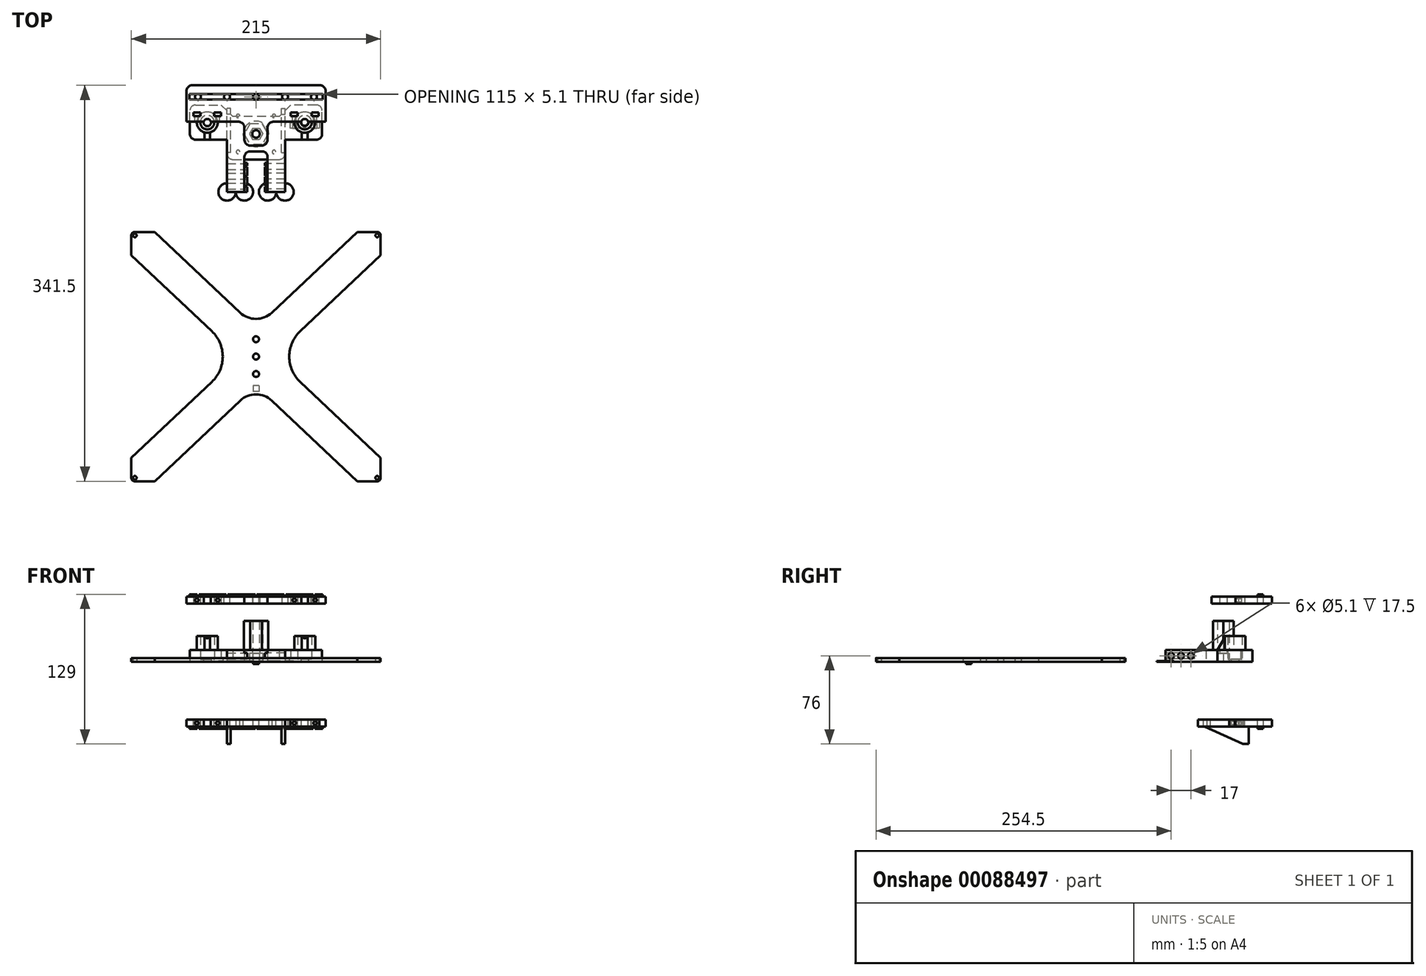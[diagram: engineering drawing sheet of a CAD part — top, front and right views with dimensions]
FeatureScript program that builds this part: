
annotation { "Feature Type Name" : "Feature", "Feature Type Description" : "" }
export const myFeature = defineFeature(function(context is Context, id is Id, definition is map)
    precondition{}
    {
        {
            var Q0;
            Q0=qCreatedBy(makeId("Top.planeOp"),FACE);
            var sketch = newSketch(context, id + "F0", { "sketchPlane" : qUnion([Q0])});
            skArc(sketch, "E0", {"start": v(0, -3.25) * mm, "mid": v(3.25, 0) * mm, "end": v(0, 3.25) * mm});
            skCircle(sketch, "E1", {"center": v(42, 10) * mm, "radius": 3.25 * mm});
            skLineSegment(sketch, "E2", {"start": v(0, -15) * mm, "end": v(5, -15) * mm});
            skLineSegment(sketch, "E3", {"start": v(10, -20) * mm, "end": v(10, -50) * mm});
            skLineSegment(sketch, "E4", {"start": v(10, -50) * mm, "end": v(25, -50) * mm});
            skLineSegment(sketch, "E5", {"start": v(25, -50) * mm, "end": v(25, -5) * mm});
            skLineSegment(sketch, "E6", {"start": v(25, -5) * mm, "end": v(52, -5) * mm});
            skLineSegment(sketch, "E7", {"start": v(57, 0) * mm, "end": v(57, 20) * mm});
            skLineSegment(sketch, "E8", {"start": v(52, 25) * mm, "end": v(30, 25) * mm});
            skLineSegment(sketch, "E9", {"start": v(30, 25) * mm, "end": v(20, 15) * mm});
            skLineSegment(sketch, "E10", {"start": v(20, 15) * mm, "end": v(0, 15) * mm});
            skPoint(sketch, "E11.visualSharp", {"position": v(10, -15) * mm});
            skArc(sketch, "E11.filletArc", {"start": v(10, -20) * mm, "mid": v(8.54, -16.46) * mm, "end": v(5, -15) * mm});
            skLineSegment(sketch, "E12", {"start": v(0, 15) * mm, "end": v(0, 3.25) * mm});
            skCircle(sketch, "E13.cCircle", {"center": v(0, 0) * mm, "radius": 5 * mm, "construction": true});
            skLineSegment(sketch, "E13.0", {"start": v(-2.89, 5) * mm, "end": v(2.89, 5) * mm, "construction": true});
            skLineSegment(sketch, "E13.1", {"start": v(2.89, 5) * mm, "end": v(5.77, 0) * mm, "construction": true});
            skLineSegment(sketch, "E13.2", {"start": v(5.77, 0) * mm, "end": v(2.89, -5) * mm, "construction": true});
            skLineSegment(sketch, "E13.3", {"start": v(2.89, -5) * mm, "end": v(-2.89, -5) * mm, "construction": true});
            skLineSegment(sketch, "E13.4", {"start": v(-2.89, -5) * mm, "end": v(-5.77, 0) * mm, "construction": true});
            skLineSegment(sketch, "E13.5", {"start": v(-5.77, 0) * mm, "end": v(-2.89, 5) * mm, "construction": true});
            skPoint(sketch, "E13.0.midPoint", {"position": v(0, 5) * mm});
            skLineSegment(sketch, "E14.trimOffspring", {"start": v(0, -3.25) * mm, "end": v(0, -15) * mm});
            skPoint(sketch, "E15.visualSharp", {"position": v(57, -5) * mm});
            skArc(sketch, "E15.filletArc", {"start": v(52, -5) * mm, "mid": v(55.54, -3.54) * mm, "end": v(57, 0) * mm});
            skPoint(sketch, "E16.visualSharp", {"position": v(57, 25) * mm});
            skArc(sketch, "E16.filletArc", {"start": v(57, 20) * mm, "mid": v(55.54, 23.54) * mm, "end": v(52, 25) * mm});
            skSolve(sketch);
        }
        {
            var Q0;
            Q0=makeQuery(id+"F0.imprint","IMPRINT",FACE,{"disambiguationData":[TD([[makeQuery(id+"F0.imprint","IMPRINT",EDGE,{"derivedFrom":sQuery(id+"F0.wireOp",EDGE,"E0")}),-1.0]])]});
            extrude(context, id + "F1", {"entities" : qUnion([Q0]), "depth" : 10 * mm});
        }
        {
            var Q0;
            Q0=makeQuery(id+"F1.opExtrude","CAP_FACE",FACE,{"disambiguationData":[OSD([sQuery(id+"F0.wireOp",EDGE,"E0"),sQuery(id+"F0.wireOp",EDGE,"E1"),sQuery(id+"F0.wireOp",EDGE,"E2"),sQuery(id+"F0.wireOp",EDGE,"E3"),sQuery(id+"F0.wireOp",EDGE,"E4"),sQuery(id+"F0.wireOp",EDGE,"E5"),sQuery(id+"F0.wireOp",EDGE,"E6"),sQuery(id+"F0.wireOp",EDGE,"E7"),sQuery(id+"F0.wireOp",EDGE,"E8"),sQuery(id+"F0.wireOp",EDGE,"E9"),sQuery(id+"F0.wireOp",EDGE,"E10"),sQuery(id+"F0.wireOp",EDGE,"E11.filletArc"),sQuery(id+"F0.wireOp",EDGE,"E12"),sQuery(id+"F0.wireOp",EDGE,"E14.trimOffspring"),sQuery(id+"F0.wireOp",EDGE,"E15.filletArc"),sQuery(id+"F0.wireOp",EDGE,"E16.filletArc")])],"isStart":false});
            var sketch = newSketch(context, id + "F2", { "sketchPlane" : qUnion([Q0])});
            skCircle(sketch, "E17", {"center": v(42, 10) * mm, "radius": 6.05 * mm});
            skCircle(sketch, "E18", {"center": v(42, 10) * mm, "radius": 9 * mm});
            skSolve(sketch);
        }
        {
            var Q0;
            Q0 = qSketchRegion(id + "F2", true);
            extrude(context, id + "F3", {"entities" : qUnion([Q0]), "operationType" : NewBodyOperationType.ADD, "depth" : 12 * mm});
        }
        {
            var Q0;
            {var subQ0=sQuery(id+"F0.wireOp",EDGE,"E9");var subQ1=sQuery(id+"F0.wireOp",EDGE,"E8");var subQ2=sQuery(id+"F0.wireOp",EDGE,"E16.filletArc");var subQ3=sQuery(id+"F0.wireOp",EDGE,"E7");var subQ4=sQuery(id+"F0.wireOp",EDGE,"E15.filletArc");var subQ5=sQuery(id+"F0.wireOp",EDGE,"E6");var subQ6=sQuery(id+"F0.wireOp",EDGE,"E5");var subQ7=sQuery(id+"F0.wireOp",EDGE,"E0");var subQ8=sQuery(id+"F0.wireOp",EDGE,"E2");var subQ9=sQuery(id+"F0.wireOp",EDGE,"E10");var subQ10=sQuery(id+"F0.wireOp",EDGE,"E3");var subQ11=sQuery(id+"F0.wireOp",EDGE,"E4");var subQ12=sQuery(id+"F0.wireOp",EDGE,"E11.filletArc");var subQ13=sQuery(id+"F0.wireOp",EDGE,"E12");var subQ14=sQuery(id+"F0.wireOp",EDGE,"E14.trimOffspring");Q0=makeQuery(id+"F3.boolean.opBoolean","SPLIT",FACE,{"disambiguationData":[TD([makeQuery(id+"F1.opExtrude","SWEPT_FACE",FACE,{"disambiguationData":[OSD([subQ7])]})])],"derivedFrom":makeQuery(id+"F1.opExtrude","CAP_FACE",FACE,{"disambiguationData":[OSD([subQ7,sQuery(id+"F0.wireOp",EDGE,"E1"),subQ8,subQ10,subQ11,subQ6,subQ5,subQ3,subQ1,subQ0,subQ9,subQ12,subQ13,subQ14,subQ4,subQ2])],"isStart":false})});}
            var sketch = newSketch(context, id + "F4", { "sketchPlane" : qUnion([Q0])});
            skArc(sketch, "E19.cCircle", {"start": v(0, -5) * mm, "mid": v(4.33, -2.5) * mm, "end": v(4.33, 2.5) * mm, "construction": true});
            skLineSegment(sketch, "E19.0", {"start": v(0, 5) * mm, "end": v(2.89, 5) * mm});
            skLineSegment(sketch, "E19.1", {"start": v(2.89, 5) * mm, "end": v(5.77, 0) * mm});
            skLineSegment(sketch, "E19.2", {"start": v(5.77, 0) * mm, "end": v(2.89, -5) * mm});
            skLineSegment(sketch, "E19.3", {"start": v(2.89, -5) * mm, "end": v(0, -5) * mm});
            skPoint(sketch, "E19.0.midPoint", {"position": v(0, 5) * mm});
            skArc(sketch, "E20.cCircle", {"start": v(0, -9) * mm, "mid": v(9, 0) * mm, "end": v(0, 9) * mm, "construction": true});
            skLineSegment(sketch, "E20.0", {"start": v(0, 9) * mm, "end": v(5.2, 9) * mm});
            skLineSegment(sketch, "E20.1", {"start": v(5.2, 9) * mm, "end": v(10.4, 0) * mm});
            skLineSegment(sketch, "E20.2", {"start": v(10.4, 0) * mm, "end": v(5.2, -9) * mm});
            skLineSegment(sketch, "E20.3", {"start": v(5.2, -9) * mm, "end": v(0, -9) * mm});
            skPoint(sketch, "E20.0.midPoint", {"position": v(0, 9) * mm});
            skLineSegment(sketch, "E21", {"start": v(0, 9) * mm, "end": v(0, 5) * mm});
            skLineSegment(sketch, "E22", {"start": v(0, -9.12) * mm, "end": v(0, -5) * mm});
            skSolve(sketch);
        }
        {
            var Q0;
            Q0 = qSketchRegion(id + "F4", true);
            extrude(context, id + "F5", {"entities" : qUnion([Q0]), "operationType" : NewBodyOperationType.ADD, "depth" : 25 * mm});
        }
        {
            var Q0;
            {var subQ0=sQuery(id+"F0.wireOp",EDGE,"E11.filletArc");var subQ2=sQuery(id+"F0.wireOp",EDGE,"E9");var subQ4=sQuery(id+"F0.wireOp",EDGE,"E8");var subQ6=sQuery(id+"F0.wireOp",EDGE,"E16.filletArc");var subQ8=sQuery(id+"F0.wireOp",EDGE,"E7");var subQ10=sQuery(id+"F0.wireOp",EDGE,"E15.filletArc");var subQ12=sQuery(id+"F0.wireOp",EDGE,"E6");var subQ14=sQuery(id+"F0.wireOp",EDGE,"E2");var subQ15=makeQuery(id+"F1.opExtrude","SWEPT_FACE",FACE,{"disambiguationData":[OSD([subQ14])]});var subQ16=sQuery(id+"F0.wireOp",EDGE,"E10");var subQ18=sQuery(id+"F0.wireOp",EDGE,"E3");var subQ20=sQuery(id+"F0.wireOp",EDGE,"E4");var subQ22=sQuery(id+"F0.wireOp",EDGE,"E5");var subQ24=sQuery(id+"F0.wireOp",EDGE,"E12");var subQ26=sQuery(id+"F0.wireOp",EDGE,"E14.trimOffspring");var subQ29=sQuery(id+"F0.wireOp",EDGE,"E0");Q0=makeQuery(id+"F5.boolean.opBoolean","SPLIT",FACE,{"disambiguationData":[TD([subQ15])],"derivedFrom":makeQuery(id+"F3.boolean.opBoolean","SPLIT",FACE,{"disambiguationData":[TD([makeQuery(id+"F1.opExtrude","SWEPT_FACE",FACE,{"disambiguationData":[OSD([subQ29])]})])],"derivedFrom":makeQuery(id+"F1.opExtrude","CAP_FACE",FACE,{"disambiguationData":[OSD([subQ29,sQuery(id+"F0.wireOp",EDGE,"E1"),subQ14,subQ18,subQ20,subQ22,subQ12,subQ8,subQ4,subQ2,subQ16,subQ0,subQ24,subQ26,subQ10,subQ6])],"isStart":false})})});}
            var sketch = newSketch(context, id + "F6", { "sketchPlane" : qUnion([Q0])});
            skCircle(sketch, "E23.0", {"center": v(42, 10) * mm, "radius": 6.05 * mm});
            skLineSegment(sketch, "E24.0", {"start": v(0, 5) * mm, "end": v(2.89, 5) * mm});
            skLineSegment(sketch, "E25.0", {"start": v(2.89, 5) * mm, "end": v(5.77, 0) * mm});
            skLineSegment(sketch, "E26.0", {"start": v(5.77, 0) * mm, "end": v(2.89, -5) * mm});
            skLineSegment(sketch, "E27.0", {"start": v(2.89, -5) * mm, "end": v(0, -5) * mm});
            skLineSegment(sketch, "E28", {"start": v(0, 5) * mm, "end": v(0, -5) * mm});
            skSolve(sketch);
        }
        {
            var Q0;
            Q0=makeQuery(id+"F6.imprint","IMPRINT",FACE,{"disambiguationData":[TD([[makeQuery(id+"F6.imprint","IMPRINT",EDGE,{"derivedFrom":sQuery(id+"F6.wireOp",EDGE,"E23.0")}),1.0]])]});
            extrude(context, id + "F7", {"entities" : qUnion([Q0]), "operationType" : NewBodyOperationType.REMOVE, "oppositeDirection" : true, "depth" : 8 * mm});
        }
        {
            var Q0;
            Q0=qCreatedBy(makeId("Right.planeOp"),FACE);
            cPlane(context, id + "F8", {"entities" : qUnion([Q0]), "cplaneType" : CPlaneType.OFFSET, "offset" : 42 * mm, "width" : 150 * mm, "height" : 150 * mm});
        }
        {
            var Q0;
            Q0=makeQuery(id+"F1.opExtrude","CAP_FACE",FACE,{"disambiguationData":[OSD([sQuery(id+"F0.wireOp",EDGE,"E0"),sQuery(id+"F0.wireOp",EDGE,"E1"),sQuery(id+"F0.wireOp",EDGE,"E2"),sQuery(id+"F0.wireOp",EDGE,"E3"),sQuery(id+"F0.wireOp",EDGE,"E4"),sQuery(id+"F0.wireOp",EDGE,"E5"),sQuery(id+"F0.wireOp",EDGE,"E6"),sQuery(id+"F0.wireOp",EDGE,"E7"),sQuery(id+"F0.wireOp",EDGE,"E8"),sQuery(id+"F0.wireOp",EDGE,"E9"),sQuery(id+"F0.wireOp",EDGE,"E10"),sQuery(id+"F0.wireOp",EDGE,"E11.filletArc"),sQuery(id+"F0.wireOp",EDGE,"E12"),sQuery(id+"F0.wireOp",EDGE,"E14.trimOffspring"),sQuery(id+"F0.wireOp",EDGE,"E15.filletArc"),sQuery(id+"F0.wireOp",EDGE,"E16.filletArc")])],"isStart":true});
            var sketch = newSketch(context, id + "F9", { "sketchPlane" : qUnion([Q0])});
            skLineSegment(sketch, "E29.0.0", {"start": v(0, 5) * mm, "end": v(2.89, 5) * mm});
            skLineSegment(sketch, "E29.0.1", {"start": v(2.89, 5) * mm, "end": v(5.77, 0) * mm});
            skLineSegment(sketch, "E29.0.2", {"start": v(5.77, 0) * mm, "end": v(2.89, -5) * mm});
            skLineSegment(sketch, "E29.0.3", {"start": v(2.89, -5) * mm, "end": v(0, -5) * mm});
            skLineSegment(sketch, "E29.0.4", {"start": v(0, -5) * mm, "end": v(0, -3.25) * mm});
            skArc(sketch, "E29.0.5", {"start": v(0, -3.25) * mm, "mid": v(3.25, 0) * mm, "end": v(0, 3.25) * mm});
            skLineSegment(sketch, "E29.0.6", {"start": v(0, 3.25) * mm, "end": v(0, 5) * mm});
            skSolve(sketch);
        }
        {
            var Q0;
            Q0=makeQuery(id+"F9.imprint","IMPRINT",FACE,{"disambiguationData":[TD([[makeQuery(id+"F9.imprint","IMPRINT",EDGE,{"derivedFrom":sQuery(id+"F9.wireOp",EDGE,"E29.0.0")}),-1.0]])]});
            extrude(context, id + "F10", {"entities" : qUnion([Q0]), "operationType" : NewBodyOperationType.REMOVE, "oppositeDirection" : true, "depth" : 7 * mm});
        }
        {
            var Q0;
            Q0=qCreatedBy(id+"F8.planeOp",FACE);
            var sketch = newSketch(context, id + "F11", { "sketchPlane" : qUnion([Q0])});
            skLineSegment(sketch, "E30", {"start": v(2, 22) * mm, "end": v(-4.93, 10) * mm});
            skLineSegment(sketch, "E31", {"start": v(-4.93, 10) * mm, "end": v(2, 10) * mm});
            skLineSegment(sketch, "E32", {"start": v(2, 10) * mm, "end": v(2, 22) * mm});
            skSolve(sketch);
        }
        {
            var Q0;
            Q0=makeQuery(id+"F11.imprint","IMPRINT",FACE,{"disambiguationData":[TD([[makeQuery(id+"F11.imprint","IMPRINT",EDGE,{"derivedFrom":sQuery(id+"F11.wireOp",EDGE,"E30")}),1.0]])]});
            extrude(context, id + "F12", {"entities" : qUnion([Q0]), "operationType" : NewBodyOperationType.ADD, "endBound" : BoundingType.SYMMETRIC, "depth" : 5 * mm});
        }
        {
            var Q0;
            Q0=makeQuery(id+"F1.opExtrude","SWEPT_FACE",FACE,{"disambiguationData":[OSD([sQuery(id+"F0.wireOp",EDGE,"E4")])]});
            var sketch = newSketch(context, id + "F13", { "sketchPlane" : qUnion([Q0])});
            skLineSegment(sketch, "E33.bottom", {"start": v(10, 7.5) * mm, "end": v(7.5, 7.5) * mm});
            skLineSegment(sketch, "E33.top", {"start": v(10, 2.5) * mm, "end": v(7.5, 2.5) * mm});
            skLineSegment(sketch, "E33.left", {"start": v(10, 7.5) * mm, "end": v(10, 2.5) * mm});
            skLineSegment(sketch, "E33.right", {"start": v(7.5, 7.5) * mm, "end": v(7.5, 2.5) * mm});
            skSolve(sketch);
        }
        {
            var Q0;
            Q0 = qSketchRegion(id + "F13", true);
            extrude(context, id + "F14", {"entities" : qUnion([Q0]), "operationType" : NewBodyOperationType.ADD, "oppositeDirection" : true, "depth" : 25 * mm});
        }
        {
            var Q0;
            Q0=makeQuery(id+"F14.opExtrude","SWEPT_FACE",FACE,{"disambiguationData":[OSD([sQuery(id+"F13.wireOp",EDGE,"E33.right")])]});
            var sketch = newSketch(context, id + "F15", { "sketchPlane" : qUnion([Q0])});
            skCircle(sketch, "E34", {"center": v(45, 5) * mm, "radius": 2.55 * mm});
            skPoint(sketch, "E34.centerSnap0", {"position": v(50, 5) * mm});
            skCircle(sketch, "E35.1.0.0", {"center": v(36.5, 5) * mm, "radius": 2.55 * mm});
            skCircle(sketch, "E35.2.0.0", {"center": v(28, 5) * mm, "radius": 2.55 * mm});
            skLineSegment(sketch, "E35.direction1", {"start": v(45, 5) * mm, "end": v(36.5, 5) * mm, "construction": true});
            skSolve(sketch);
        }
        {
            var Q0;
            Q0 = qSketchRegion(id + "F15", true);
            extrude(context, id + "F16", {"entities" : qUnion([Q0]), "operationType" : NewBodyOperationType.REMOVE, "oppositeDirection" : true, "depth" : 25 * mm});
        }
        {
            var Q0;
            Q0=makeQuery(id+"F1.opExtrude","SWEPT_BODY",BODY,{"disambiguationData":[OSD([sQuery(id+"F0.wireOp",EDGE,"E0"),sQuery(id+"F0.wireOp",EDGE,"E1"),sQuery(id+"F0.wireOp",EDGE,"E2"),sQuery(id+"F0.wireOp",EDGE,"E3"),sQuery(id+"F0.wireOp",EDGE,"E4"),sQuery(id+"F0.wireOp",EDGE,"E5"),sQuery(id+"F0.wireOp",EDGE,"E6"),sQuery(id+"F0.wireOp",EDGE,"E7"),sQuery(id+"F0.wireOp",EDGE,"E8"),sQuery(id+"F0.wireOp",EDGE,"E9"),sQuery(id+"F0.wireOp",EDGE,"E10"),sQuery(id+"F0.wireOp",EDGE,"E11.filletArc"),sQuery(id+"F0.wireOp",EDGE,"E12"),sQuery(id+"F0.wireOp",EDGE,"E14.trimOffspring"),sQuery(id+"F0.wireOp",EDGE,"E15.filletArc"),sQuery(id+"F0.wireOp",EDGE,"E16.filletArc")])]});
            var Q1;
            Q1=qCreatedBy(makeId("Right.planeOp"),FACE);
            mirror(context, id + "F17", {"operationType" : NewBodyOperationType.ADD, "entities" : qUnion([Q0]), "mirrorPlane" : qUnion([Q1])});
        }
        {
            var Q0;
            Q0=qCreatedBy(makeId("Top.planeOp"),FACE);
            cPlane(context, id + "F18", {"entities" : qUnion([Q0]), "cplaneType" : CPlaneType.OFFSET, "offset" : 50 * mm, "width" : 150 * mm, "height" : 150 * mm});
        }
        {
            var Q0;
            Q0=qCreatedBy(id+"F18.planeOp",FACE);
            var sketch = newSketch(context, id + "F19", { "sketchPlane" : qUnion([Q0])});
            skArc(sketch, "E36.0", {"start": v(-39.04, 10.5) * mm, "mid": v(-42, 13) * mm, "end": v(-44.96, 10.5) * mm});
            skCircle(sketch, "E37.0", {"center": v(0, 0) * mm, "radius": 3.25 * mm});
            skArc(sketch, "E38.0", {"start": v(44.96, 10.5) * mm, "mid": v(42, 13) * mm, "end": v(39.04, 10.5) * mm});
            skLineSegment(sketch, "E39", {"start": v(-60, 10.5) * mm, "end": v(-60, 37) * mm});
            skLineSegment(sketch, "E40", {"start": v(-55, 42) * mm, "end": v(55, 42) * mm});
            skLineSegment(sketch, "E41", {"start": v(60, 37) * mm, "end": v(60, 10.5) * mm});
            skArc(sketch, "E42.filletArc", {"start": v(-55, 42) * mm, "mid": v(-58.54, 40.54) * mm, "end": v(-60, 37) * mm});
            skPoint(sketch, "E43.visualSharp", {"position": v(60, 42) * mm});
            skArc(sketch, "E43.filletArc", {"start": v(60, 37) * mm, "mid": v(58.54, 40.54) * mm, "end": v(55, 42) * mm});
            skLineSegment(sketch, "E44", {"start": v(-10, 5.5) * mm, "end": v(-10, -5) * mm});
            skLineSegment(sketch, "E45", {"start": v(-5, -10) * mm, "end": v(5, -10) * mm});
            skLineSegment(sketch, "E46", {"start": v(10, -5) * mm, "end": v(10, 5.5) * mm});
            skLineSegment(sketch, "E47", {"start": v(15, 10.5) * mm, "end": v(39.04, 10.5) * mm});
            skLineSegment(sketch, "E48", {"start": v(-15, 10.5) * mm, "end": v(-39.04, 10.5) * mm});
            skLineSegment(sketch, "E49", {"start": v(0, 0) * mm, "end": v(0, -10) * mm, "construction": true});
            skLineSegment(sketch, "E50", {"start": v(60, 10.5) * mm, "end": v(44.96, 10.5) * mm});
            skLineSegment(sketch, "E51", {"start": v(-60, 10.5) * mm, "end": v(-44.96, 10.5) * mm});
            skLineSegment(sketch, "E52.bottom", {"start": v(-54, 18.5) * mm, "end": v(-48, 18.5) * mm});
            skLineSegment(sketch, "E52.top", {"start": v(-54, 15.5) * mm, "end": v(-48, 15.5) * mm});
            skLineSegment(sketch, "E52.left", {"start": v(-54, 18.5) * mm, "end": v(-54, 15.5) * mm});
            skLineSegment(sketch, "E52.right", {"start": v(-48, 18.5) * mm, "end": v(-48, 15.5) * mm});
            skLineSegment(sketch, "E53", {"start": v(-42, 10) * mm, "end": v(-42, 18.5) * mm, "construction": true});
            skLineSegment(sketch, "E54", {"start": v(-51, 18.5) * mm, "end": v(-51, 15.5) * mm, "construction": true});
            skLineSegment(sketch, "E55.MirrorCS", {"start": v(-36, 18.5) * mm, "end": v(-36, 15.5) * mm});
            skLineSegment(sketch, "E56.MirrorCS", {"start": v(-30, 18.5) * mm, "end": v(-36, 18.5) * mm});
            skLineSegment(sketch, "E57.MirrorCS", {"start": v(-30, 18.5) * mm, "end": v(-30, 15.5) * mm});
            skLineSegment(sketch, "E58.MirrorCS", {"start": v(-30, 15.5) * mm, "end": v(-36, 15.5) * mm});
            skLineSegment(sketch, "E59.MirrorCS", {"start": v(30, 15.5) * mm, "end": v(36, 15.5) * mm});
            skLineSegment(sketch, "E60.MirrorCS", {"start": v(30, 18.5) * mm, "end": v(36, 18.5) * mm});
            skLineSegment(sketch, "E61.MirrorCS", {"start": v(30, 18.5) * mm, "end": v(30, 15.5) * mm});
            skLineSegment(sketch, "E62.MirrorCS", {"start": v(36, 18.5) * mm, "end": v(36, 15.5) * mm});
            skLineSegment(sketch, "E63.MirrorCS", {"start": v(48, 18.5) * mm, "end": v(48, 15.5) * mm});
            skLineSegment(sketch, "E64.MirrorCS", {"start": v(54, 18.5) * mm, "end": v(48, 18.5) * mm});
            skLineSegment(sketch, "E65.MirrorCS", {"start": v(54, 18.5) * mm, "end": v(54, 15.5) * mm});
            skLineSegment(sketch, "E66.MirrorCS", {"start": v(54, 15.5) * mm, "end": v(48, 15.5) * mm});
            skPoint(sketch, "E67.visualSharp", {"position": v(-10, 10.5) * mm});
            skArc(sketch, "E67.filletArc", {"start": v(-10, 5.5) * mm, "mid": v(-11.46, 9.04) * mm, "end": v(-15, 10.5) * mm});
            skPoint(sketch, "E68.visualSharp", {"position": v(10, 10.5) * mm});
            skArc(sketch, "E68.filletArc", {"start": v(15, 10.5) * mm, "mid": v(11.46, 9.04) * mm, "end": v(10, 5.5) * mm});
            skPoint(sketch, "E69.visualSharp", {"position": v(10, -10) * mm});
            skArc(sketch, "E69.filletArc", {"start": v(5, -10) * mm, "mid": v(8.54, -8.54) * mm, "end": v(10, -5) * mm});
            skPoint(sketch, "E70.visualSharp", {"position": v(-10, -10) * mm});
            skArc(sketch, "E70.filletArc", {"start": v(-10, -5) * mm, "mid": v(-8.54, -8.54) * mm, "end": v(-5, -10) * mm});
            skSolve(sketch);
        }
        {
            var Q0;
            Q0=makeQuery(id+"F19.imprint","IMPRINT",FACE,{"disambiguationData":[TD([[makeQuery(id+"F19.imprint","IMPRINT",EDGE,{"derivedFrom":sQuery(id+"F19.wireOp",EDGE,"E36.0")}),-1.0]])]});
            extrude(context, id + "F20", {"entities" : qUnion([Q0]), "depth" : 6 * mm});
        }
        {
            var Q0;
            Q0=makeQuery(id+"F20.opExtrude","SWEPT_FACE",FACE,{"disambiguationData":[OSD([sQuery(id+"F19.wireOp",EDGE,"E52.top")])]});
            var sketch = newSketch(context, id + "F21", { "sketchPlane" : qUnion([Q0])});
            skCircle(sketch, "E71", {"center": v(51, 53) * mm, "radius": 1.55 * mm});
            skPoint(sketch, "E71.centerSnap0", {"position": v(51, 56) * mm});
            skLineSegment(sketch, "E72", {"start": v(54, 53) * mm, "end": v(51, 53) * mm, "construction": true});
            skCircle(sketch, "E73", {"center": v(33, 53) * mm, "radius": 1.55 * mm});
            skLineSegment(sketch, "E74", {"start": v(0, 59.79) * mm, "end": v(0, 45.57) * mm, "construction": true});
            skCircle(sketch, "E75.MirrorC", {"center": v(-33, 53) * mm, "radius": 1.55 * mm});
            skCircle(sketch, "E76.MirrorC", {"center": v(-51, 53) * mm, "radius": 1.55 * mm});
            skSolve(sketch);
        }
        {
            var Q0;
            Q0 = qSketchRegion(id + "F21", true);
            extrude(context, id + "F22", {"entities" : qUnion([Q0]), "operationType" : NewBodyOperationType.REMOVE, "oppositeDirection" : true, "depth" : 10 * mm});
        }
        {
            var Q0;
            Q0=qCreatedBy(makeId("Right.planeOp"),FACE);
            var sketch = newSketch(context, id + "F23", { "sketchPlane" : qUnion([Q0])});
            skLineSegment(sketch, "E77", {"start": v(29.55, 56) * mm, "end": v(29.55, 58) * mm});
            skLineSegment(sketch, "E78", {"start": v(29.55, 58) * mm, "end": v(34.45, 58) * mm});
            skLineSegment(sketch, "E79", {"start": v(34.45, 58) * mm, "end": v(34.45, 56) * mm});
            skPoint(sketch, "E80", {"position": v(32, 58) * mm});
            skLineSegment(sketch, "E81", {"start": v(29.55, 56) * mm, "end": v(34.45, 56) * mm});
            skSolve(sketch);
        }
        {
            var Q0;
            Q0=makeQuery(id+"F23.imprint","IMPRINT",FACE,{"disambiguationData":[TD([[makeQuery(id+"F23.imprint","IMPRINT",EDGE,{"derivedFrom":sQuery(id+"F23.wireOp",EDGE,"E77")}),-1.0]])]});
            extrude(context, id + "F24", {"entities" : qUnion([Q0]), "operationType" : NewBodyOperationType.ADD, "endBound" : BoundingType.SYMMETRIC, "depth" : 115 * mm});
        }
        {
            var Q0;
            Q0=makeQuery(id+"F24.opExtrude","SWEPT_FACE",FACE,{"disambiguationData":[OSD([sQuery(id+"F23.wireOp",EDGE,"E78")])]});
            var sketch = newSketch(context, id + "F25", { "sketchPlane" : qUnion([Q0])});
            skCircle(sketch, "E82", {"center": v(0, 32) * mm, "radius": 2.55 * mm});
            skCircle(sketch, "E83", {"center": v(25, 32) * mm, "radius": 2.55 * mm});
            skCircle(sketch, "E84", {"center": v(50, 32) * mm, "radius": 2.55 * mm});
            skCircle(sketch, "E85", {"center": v(-25, 32) * mm, "radius": 2.55 * mm});
            skCircle(sketch, "E86", {"center": v(-50, 32) * mm, "radius": 2.55 * mm});
            skLineSegment(sketch, "E87", {"start": v(-50, 32) * mm, "end": v(-25, 32) * mm, "construction": true});
            skLineSegment(sketch, "E88", {"start": v(-25, 32) * mm, "end": v(0, 32) * mm, "construction": true});
            skLineSegment(sketch, "E89", {"start": v(25, 32) * mm, "end": v(0, 32) * mm, "construction": true});
            skLineSegment(sketch, "E90", {"start": v(50, 32) * mm, "end": v(25, 32) * mm, "construction": true});
            skSolve(sketch);
        }
        {
            var Q0;
            Q0 = qSketchRegion(id + "F25", true);
            extrude(context, id + "F26", {"entities" : qUnion([Q0]), "operationType" : NewBodyOperationType.REMOVE, "oppositeDirection" : true, "depth" : 10 * mm});
        }
        {
            var Q0;
            Q0=qCreatedBy(makeId("Top.planeOp"),FACE);
            cPlane(context, id + "F27", {"entities" : qUnion([Q0]), "cplaneType" : CPlaneType.OFFSET, "offset" : 50 * mm, "oppositeDirection" : true, "width" : 150 * mm, "height" : 150 * mm});
        }
        {
            var Q0;
            Q0=qCreatedBy(id+"F27.planeOp",FACE);
            var sketch = newSketch(context, id + "F28", { "sketchPlane" : qUnion([Q0])});
            skArc(sketch, "E91.0", {"start": v(-39.04, 10.5) * mm, "mid": v(-42, 13) * mm, "end": v(-44.96, 10.5) * mm});
            skLineSegment(sketch, "E92.0", {"start": v(-60, 10.5) * mm, "end": v(-44.96, 10.5) * mm});
            skArc(sketch, "E93.0", {"start": v(44.96, 10.5) * mm, "mid": v(42, 13) * mm, "end": v(39.04, 10.5) * mm});
            skLineSegment(sketch, "E94.0", {"start": v(60, 10.5) * mm, "end": v(44.96, 10.5) * mm});
            skLineSegment(sketch, "E95.0", {"start": v(60, 37) * mm, "end": v(60, 10.5) * mm});
            skArc(sketch, "E96.0", {"start": v(60, 37) * mm, "mid": v(58.54, 40.54) * mm, "end": v(55, 42) * mm});
            skLineSegment(sketch, "E97.0", {"start": v(-55, 42) * mm, "end": v(55, 42) * mm});
            skArc(sketch, "E98.0", {"start": v(-55, 42) * mm, "mid": v(-58.54, 40.54) * mm, "end": v(-60, 37) * mm});
            skLineSegment(sketch, "E99.0", {"start": v(-60, 10.5) * mm, "end": v(-60, 37) * mm});
            skLineSegment(sketch, "E100.0", {"start": v(-54, 18.5) * mm, "end": v(-48, 18.5) * mm});
            skLineSegment(sketch, "E101.0", {"start": v(-48, 18.5) * mm, "end": v(-48, 15.5) * mm});
            skLineSegment(sketch, "E102.0", {"start": v(-54, 15.5) * mm, "end": v(-48, 15.5) * mm});
            skLineSegment(sketch, "E103.0", {"start": v(-54, 18.5) * mm, "end": v(-54, 15.5) * mm});
            skLineSegment(sketch, "E104.0", {"start": v(-30, 18.5) * mm, "end": v(-36, 18.5) * mm});
            skLineSegment(sketch, "E105.0", {"start": v(-36, 18.5) * mm, "end": v(-36, 15.5) * mm});
            skLineSegment(sketch, "E106.0", {"start": v(-30, 15.5) * mm, "end": v(-36, 15.5) * mm});
            skLineSegment(sketch, "E107.0", {"start": v(-30, 18.5) * mm, "end": v(-30, 15.5) * mm});
            skLineSegment(sketch, "E108.0", {"start": v(30, 18.5) * mm, "end": v(30, 15.5) * mm});
            skLineSegment(sketch, "E109.0", {"start": v(30, 18.5) * mm, "end": v(36, 18.5) * mm});
            skLineSegment(sketch, "E110.0", {"start": v(36, 18.5) * mm, "end": v(36, 15.5) * mm});
            skLineSegment(sketch, "E111.0", {"start": v(30, 15.5) * mm, "end": v(36, 15.5) * mm});
            skLineSegment(sketch, "E112.0", {"start": v(48, 18.5) * mm, "end": v(48, 15.5) * mm});
            skLineSegment(sketch, "E113.0", {"start": v(54, 18.5) * mm, "end": v(48, 18.5) * mm});
            skLineSegment(sketch, "E114.0", {"start": v(54, 18.5) * mm, "end": v(54, 15.5) * mm});
            skLineSegment(sketch, "E115.0", {"start": v(54, 15.5) * mm, "end": v(48, 15.5) * mm});
            skCircle(sketch, "E116", {"center": v(0, 0) * mm, "radius": 11 * mm});
            skLineSegment(sketch, "E117.bottom", {"start": v(-15.5, -15.5) * mm, "end": v(15.5, -15.5) * mm, "construction": true});
            skLineSegment(sketch, "E117.top", {"start": v(-15.5, 15.5) * mm, "end": v(15.5, 15.5) * mm, "construction": true});
            skLineSegment(sketch, "E117.left", {"start": v(-15.5, -15.5) * mm, "end": v(-15.5, 15.5) * mm, "construction": true});
            skLineSegment(sketch, "E117.right", {"start": v(15.5, -15.5) * mm, "end": v(15.5, 15.5) * mm, "construction": true});
            skCircle(sketch, "E118", {"center": v(-15.5, -15.5) * mm, "radius": 1.55 * mm});
            skCircle(sketch, "E119", {"center": v(15.5, -15.5) * mm, "radius": 1.55 * mm});
            skCircle(sketch, "E120", {"center": v(15.5, 15.5) * mm, "radius": 1.55 * mm});
            skCircle(sketch, "E121", {"center": v(-15.5, 15.5) * mm, "radius": 1.55 * mm});
            skLineSegment(sketch, "E122", {"start": v(-20, -22) * mm, "end": v(20, -22) * mm});
            skPoint(sketch, "E123", {"position": v(0, -22) * mm});
            skLineSegment(sketch, "E124", {"start": v(-25, -17) * mm, "end": v(-25, 8) * mm});
            skLineSegment(sketch, "E125", {"start": v(25, -17) * mm, "end": v(25, 8) * mm});
            skLineSegment(sketch, "E126.trimOffspring", {"start": v(-27.5, 10.5) * mm, "end": v(-39.04, 10.5) * mm});
            skLineSegment(sketch, "E127.trimOffspring", {"start": v(27.5, 10.5) * mm, "end": v(39.04, 10.5) * mm});
            skPoint(sketch, "E128.visualSharp", {"position": v(-25, -22) * mm});
            skArc(sketch, "E128.filletArc", {"start": v(-25, -17) * mm, "mid": v(-23.54, -20.54) * mm, "end": v(-20, -22) * mm});
            skPoint(sketch, "E129.visualSharp", {"position": v(-25, 10.5) * mm});
            skArc(sketch, "E129.filletArc", {"start": v(-25, 8) * mm, "mid": v(-25.73, 9.77) * mm, "end": v(-27.5, 10.5) * mm});
            skPoint(sketch, "E130.visualSharp", {"position": v(25, -22) * mm});
            skArc(sketch, "E130.filletArc", {"start": v(20, -22) * mm, "mid": v(23.54, -20.54) * mm, "end": v(25, -17) * mm});
            skPoint(sketch, "E131.visualSharp", {"position": v(25, 10.5) * mm});
            skArc(sketch, "E131.filletArc", {"start": v(27.5, 10.5) * mm, "mid": v(25.73, 9.77) * mm, "end": v(25, 8) * mm});
            skSolve(sketch);
        }
        {
            var Q0;
            Q0=makeQuery(id+"F28.imprint","IMPRINT",FACE,{"disambiguationData":[TD([[makeQuery(id+"F28.imprint","IMPRINT",EDGE,{"derivedFrom":sQuery(id+"F28.wireOp",EDGE,"E91.0")}),-1.0]])]});
            extrude(context, id + "F29", {"entities" : qUnion([Q0]), "oppositeDirection" : true, "depth" : 6 * mm});
        }
        {
            var Q0;
            Q0=makeQuery(id+"F29.opExtrude","SWEPT_FACE",FACE,{"disambiguationData":[OSD([sQuery(id+"F28.wireOp",EDGE,"E102.0")])]});
            var sketch = newSketch(context, id + "F30", { "sketchPlane" : qUnion([Q0])});
            skCircle(sketch, "E132", {"center": v(51, -53) * mm, "radius": 1.55 * mm});
            skPoint(sketch, "E132.centerSnap0", {"position": v(54, -53) * mm});
            skPoint(sketch, "E132.centerSnap1", {"position": v(51, -50) * mm});
            skCircle(sketch, "E133", {"center": v(33, -53) * mm, "radius": 1.55 * mm});
            skLineSegment(sketch, "E134", {"start": v(0, -41.03) * mm, "end": v(0, -69.82) * mm, "construction": true});
            skCircle(sketch, "E135.MirrorC", {"center": v(-33, -53) * mm, "radius": 1.55 * mm});
            skCircle(sketch, "E136.MirrorC", {"center": v(-51, -53) * mm, "radius": 1.55 * mm});
            skSolve(sketch);
        }
        {
            var Q0;
            Q0 = qSketchRegion(id + "F30", true);
            extrude(context, id + "F31", {"entities" : qUnion([Q0]), "operationType" : NewBodyOperationType.REMOVE, "oppositeDirection" : true, "depth" : 10 * mm});
        }
        {
            var Q0;
            Q0=qCreatedBy(makeId("Right.planeOp"),FACE);
            var sketch = newSketch(context, id + "F32", { "sketchPlane" : qUnion([Q0])});
            skLineSegment(sketch, "E137", {"start": v(34.45, -56) * mm, "end": v(34.45, -58) * mm});
            skLineSegment(sketch, "E138", {"start": v(34.45, -58) * mm, "end": v(29.55, -58) * mm});
            skLineSegment(sketch, "E139", {"start": v(29.55, -58) * mm, "end": v(29.55, -56) * mm});
            skLineSegment(sketch, "E140", {"start": v(29.55, -56) * mm, "end": v(34.45, -56) * mm});
            skPoint(sketch, "E141", {"position": v(32, -58) * mm});
            skSolve(sketch);
        }
        {
            var Q0;
            Q0=makeQuery(id+"F32.imprint","IMPRINT",FACE,{"disambiguationData":[TD([[makeQuery(id+"F32.imprint","IMPRINT",EDGE,{"derivedFrom":sQuery(id+"F32.wireOp",EDGE,"E137")}),-1.0]])]});
            extrude(context, id + "F33", {"entities" : qUnion([Q0]), "operationType" : NewBodyOperationType.ADD, "endBound" : BoundingType.SYMMETRIC, "depth" : 115 * mm});
        }
        {
            var Q0;
            Q0=makeQuery(id+"F29.opExtrude","CAP_FACE",FACE,{"disambiguationData":[OSD([sQuery(id+"F28.wireOp",EDGE,"E91.0"),sQuery(id+"F28.wireOp",EDGE,"E92.0"),sQuery(id+"F28.wireOp",EDGE,"E93.0"),sQuery(id+"F28.wireOp",EDGE,"E94.0"),sQuery(id+"F28.wireOp",EDGE,"E95.0"),sQuery(id+"F28.wireOp",EDGE,"E96.0"),sQuery(id+"F28.wireOp",EDGE,"E97.0"),sQuery(id+"F28.wireOp",EDGE,"E98.0"),sQuery(id+"F28.wireOp",EDGE,"E99.0"),sQuery(id+"F28.wireOp",EDGE,"E100.0"),sQuery(id+"F28.wireOp",EDGE,"E101.0"),sQuery(id+"F28.wireOp",EDGE,"E102.0"),sQuery(id+"F28.wireOp",EDGE,"E103.0"),sQuery(id+"F28.wireOp",EDGE,"E104.0"),sQuery(id+"F28.wireOp",EDGE,"E105.0"),sQuery(id+"F28.wireOp",EDGE,"E106.0"),sQuery(id+"F28.wireOp",EDGE,"E107.0"),sQuery(id+"F28.wireOp",EDGE,"E108.0"),sQuery(id+"F28.wireOp",EDGE,"E109.0"),sQuery(id+"F28.wireOp",EDGE,"E110.0"),sQuery(id+"F28.wireOp",EDGE,"E111.0"),sQuery(id+"F28.wireOp",EDGE,"E112.0"),sQuery(id+"F28.wireOp",EDGE,"E113.0"),sQuery(id+"F28.wireOp",EDGE,"E114.0"),sQuery(id+"F28.wireOp",EDGE,"E115.0"),sQuery(id+"F28.wireOp",EDGE,"E116"),sQuery(id+"F28.wireOp",EDGE,"E118"),sQuery(id+"F28.wireOp",EDGE,"E119"),sQuery(id+"F28.wireOp",EDGE,"E120"),sQuery(id+"F28.wireOp",EDGE,"E121"),sQuery(id+"F28.wireOp",EDGE,"E122"),sQuery(id+"F28.wireOp",EDGE,"E124"),sQuery(id+"F28.wireOp",EDGE,"E125"),sQuery(id+"F28.wireOp",EDGE,"E126.trimOffspring"),sQuery(id+"F28.wireOp",EDGE,"E127.trimOffspring"),sQuery(id+"F28.wireOp",EDGE,"E128.filletArc"),sQuery(id+"F28.wireOp",EDGE,"E129.filletArc"),sQuery(id+"F28.wireOp",EDGE,"E130.filletArc"),sQuery(id+"F28.wireOp",EDGE,"E131.filletArc")])],"isStart":true});
            var sketch = newSketch(context, id + "F34", { "sketchPlane" : qUnion([Q0])});
            skCircle(sketch, "E142.0", {"center": v(-50, 32) * mm, "radius": 2.55 * mm});
            skCircle(sketch, "E143.0", {"center": v(-25, 32) * mm, "radius": 2.55 * mm});
            skCircle(sketch, "E144.0", {"center": v(0, 32) * mm, "radius": 2.55 * mm});
            skCircle(sketch, "E145.0", {"center": v(25, 32) * mm, "radius": 2.55 * mm});
            skCircle(sketch, "E146.0", {"center": v(50, 32) * mm, "radius": 2.55 * mm});
            skSolve(sketch);
        }
        {
            var Q0;
            Q0 = qSketchRegion(id + "F34", true);
            extrude(context, id + "F35", {"entities" : qUnion([Q0]), "operationType" : NewBodyOperationType.REMOVE, "oppositeDirection" : true, "depth" : 10 * mm});
        }
        {
            var Q0;
            Q0=makeQuery(id+"F29.opExtrude","SWEPT_FACE",FACE,{"disambiguationData":[OSD([sQuery(id+"F28.wireOp",EDGE,"E125")])]});
            var sketch = newSketch(context, id + "F36", { "sketchPlane" : qUnion([Q0])});
            skLineSegment(sketch, "E147", {"start": v(-16.1, -56) * mm, "end": v(16.9, -71) * mm});
            skLineSegment(sketch, "E148", {"start": v(16.9, -71) * mm, "end": v(21.9, -71) * mm});
            skLineSegment(sketch, "E149", {"start": v(21.9, -71) * mm, "end": v(21.9, -56) * mm});
            skLineSegment(sketch, "E150", {"start": v(-16.1, -56) * mm, "end": v(21.9, -56) * mm});
            skSolve(sketch);
        }
        {
            var Q0;
            Q0 = qSketchRegion(id + "F36", true);
            extrude(context, id + "F37", {"entities" : qUnion([Q0]), "operationType" : NewBodyOperationType.ADD, "oppositeDirection" : true, "depth" : 3 * mm});
        }
        {
            var Q0;
            Q0=makeQuery(id+"F29.opExtrude","SWEPT_BODY",BODY,{"disambiguationData":[OSD([sQuery(id+"F28.wireOp",EDGE,"E91.0"),sQuery(id+"F28.wireOp",EDGE,"E92.0"),sQuery(id+"F28.wireOp",EDGE,"E93.0"),sQuery(id+"F28.wireOp",EDGE,"E94.0"),sQuery(id+"F28.wireOp",EDGE,"E95.0"),sQuery(id+"F28.wireOp",EDGE,"E96.0"),sQuery(id+"F28.wireOp",EDGE,"E97.0"),sQuery(id+"F28.wireOp",EDGE,"E98.0"),sQuery(id+"F28.wireOp",EDGE,"E99.0"),sQuery(id+"F28.wireOp",EDGE,"E100.0"),sQuery(id+"F28.wireOp",EDGE,"E101.0"),sQuery(id+"F28.wireOp",EDGE,"E102.0"),sQuery(id+"F28.wireOp",EDGE,"E103.0"),sQuery(id+"F28.wireOp",EDGE,"E104.0"),sQuery(id+"F28.wireOp",EDGE,"E105.0"),sQuery(id+"F28.wireOp",EDGE,"E106.0"),sQuery(id+"F28.wireOp",EDGE,"E107.0"),sQuery(id+"F28.wireOp",EDGE,"E108.0"),sQuery(id+"F28.wireOp",EDGE,"E109.0"),sQuery(id+"F28.wireOp",EDGE,"E110.0"),sQuery(id+"F28.wireOp",EDGE,"E111.0"),sQuery(id+"F28.wireOp",EDGE,"E112.0"),sQuery(id+"F28.wireOp",EDGE,"E113.0"),sQuery(id+"F28.wireOp",EDGE,"E114.0"),sQuery(id+"F28.wireOp",EDGE,"E115.0"),sQuery(id+"F28.wireOp",EDGE,"E116"),sQuery(id+"F28.wireOp",EDGE,"E118"),sQuery(id+"F28.wireOp",EDGE,"E119"),sQuery(id+"F28.wireOp",EDGE,"E120"),sQuery(id+"F28.wireOp",EDGE,"E121"),sQuery(id+"F28.wireOp",EDGE,"E122"),sQuery(id+"F28.wireOp",EDGE,"E124"),sQuery(id+"F28.wireOp",EDGE,"E125"),sQuery(id+"F28.wireOp",EDGE,"E126.trimOffspring"),sQuery(id+"F28.wireOp",EDGE,"E127.trimOffspring"),sQuery(id+"F28.wireOp",EDGE,"E128.filletArc"),sQuery(id+"F28.wireOp",EDGE,"E129.filletArc"),sQuery(id+"F28.wireOp",EDGE,"E130.filletArc"),sQuery(id+"F28.wireOp",EDGE,"E131.filletArc")])]});
            var Q1;
            Q1=qCreatedBy(makeId("Right.planeOp"),FACE);
            mirror(context, id + "F38", {"operationType" : NewBodyOperationType.ADD, "entities" : qUnion([Q0]), "mirrorPlane" : qUnion([Q1])});
        }
        {
            var Q0;
            Q0=makeQuery(id+"F29.opExtrude","CAP_FACE",FACE,{"disambiguationData":[OSD([sQuery(id+"F28.wireOp",EDGE,"E91.0"),sQuery(id+"F28.wireOp",EDGE,"E92.0"),sQuery(id+"F28.wireOp",EDGE,"E93.0"),sQuery(id+"F28.wireOp",EDGE,"E94.0"),sQuery(id+"F28.wireOp",EDGE,"E95.0"),sQuery(id+"F28.wireOp",EDGE,"E96.0"),sQuery(id+"F28.wireOp",EDGE,"E97.0"),sQuery(id+"F28.wireOp",EDGE,"E98.0"),sQuery(id+"F28.wireOp",EDGE,"E99.0"),sQuery(id+"F28.wireOp",EDGE,"E100.0"),sQuery(id+"F28.wireOp",EDGE,"E101.0"),sQuery(id+"F28.wireOp",EDGE,"E102.0"),sQuery(id+"F28.wireOp",EDGE,"E103.0"),sQuery(id+"F28.wireOp",EDGE,"E104.0"),sQuery(id+"F28.wireOp",EDGE,"E105.0"),sQuery(id+"F28.wireOp",EDGE,"E106.0"),sQuery(id+"F28.wireOp",EDGE,"E107.0"),sQuery(id+"F28.wireOp",EDGE,"E108.0"),sQuery(id+"F28.wireOp",EDGE,"E109.0"),sQuery(id+"F28.wireOp",EDGE,"E110.0"),sQuery(id+"F28.wireOp",EDGE,"E111.0"),sQuery(id+"F28.wireOp",EDGE,"E112.0"),sQuery(id+"F28.wireOp",EDGE,"E113.0"),sQuery(id+"F28.wireOp",EDGE,"E114.0"),sQuery(id+"F28.wireOp",EDGE,"E115.0"),sQuery(id+"F28.wireOp",EDGE,"E116"),sQuery(id+"F28.wireOp",EDGE,"E118"),sQuery(id+"F28.wireOp",EDGE,"E119"),sQuery(id+"F28.wireOp",EDGE,"E120"),sQuery(id+"F28.wireOp",EDGE,"E121"),sQuery(id+"F28.wireOp",EDGE,"E122"),sQuery(id+"F28.wireOp",EDGE,"E124"),sQuery(id+"F28.wireOp",EDGE,"E125"),sQuery(id+"F28.wireOp",EDGE,"E126.trimOffspring"),sQuery(id+"F28.wireOp",EDGE,"E127.trimOffspring"),sQuery(id+"F28.wireOp",EDGE,"E128.filletArc"),sQuery(id+"F28.wireOp",EDGE,"E129.filletArc"),sQuery(id+"F28.wireOp",EDGE,"E130.filletArc"),sQuery(id+"F28.wireOp",EDGE,"E131.filletArc")])],"isStart":true});
            var sketch = newSketch(context, id + "F39", { "sketchPlane" : qUnion([Q0])});
            skArc(sketch, "E151", {"start": v(39, 10) * mm, "mid": v(42, 7) * mm, "end": v(45, 10) * mm});
            skLineSegment(sketch, "E152", {"start": v(45, 10) * mm, "end": v(54.5, 10) * mm});
            skLineSegment(sketch, "E153", {"start": v(54.5, 10) * mm, "end": v(54.5, 5) * mm});
            skLineSegment(sketch, "E154", {"start": v(54.5, 5) * mm, "end": v(29.5, 5) * mm});
            skLineSegment(sketch, "E155", {"start": v(29.5, 5) * mm, "end": v(29.5, 10) * mm});
            skLineSegment(sketch, "E156", {"start": v(29.5, 10) * mm, "end": v(39, 10) * mm});
            skSolve(sketch);
        }
        {
            var Q0;
            Q0 = qSketchRegion(id + "F39", true);
            extrude(context, id + "F40", {"entities" : qUnion([Q0]), "oppositeDirection" : true, "depth" : 6 * mm});
        }
        {
            var Q0;
            Q0=makeQuery(id+"F40.opExtrude","SWEPT_FACE",FACE,{"disambiguationData":[OSD([sQuery(id+"F39.wireOp",EDGE,"E154")])]});
            var sketch = newSketch(context, id + "F41", { "sketchPlane" : qUnion([Q0])});
            skCircle(sketch, "E157.0", {"center": v(33, -53) * mm, "radius": 1.55 * mm});
            skCircle(sketch, "E158.0", {"center": v(51, -53) * mm, "radius": 1.55 * mm});
            skSolve(sketch);
        }
        {
            var Q0;
            Q0 = qSketchRegion(id + "F41", true);
            extrude(context, id + "F42", {"entities" : qUnion([Q0]), "operationType" : NewBodyOperationType.REMOVE, "oppositeDirection" : true, "depth" : 6 * mm});
        }
        {
            var Q0;
            Q0=qCreatedBy(makeId("Top.planeOp"),FACE);
            var sketch = newSketch(context, id + "F43", { "sketchPlane" : qUnion([Q0])});
            skLineSegment(sketch, "E159.bottom", {"start": v(104.5, -87.5) * mm, "end": v(-104.5, -87.5) * mm, "construction": true});
            skLineSegment(sketch, "E159.top", {"start": v(104.5, -296.5) * mm, "end": v(-104.5, -296.5) * mm, "construction": true});
            skLineSegment(sketch, "E159.left", {"start": v(104.5, -87.5) * mm, "end": v(104.5, -296.5) * mm, "construction": true});
            skLineSegment(sketch, "E159.right", {"start": v(-104.5, -87.5) * mm, "end": v(-104.5, -296.5) * mm, "construction": true});
            skPoint(sketch, "E159.middle", {"position": v(0, -192) * mm});
            skCircle(sketch, "E160", {"center": v(-104.5, -87.5) * mm, "radius": 1.55 * mm});
            skCircle(sketch, "E161", {"center": v(104.5, -87.5) * mm, "radius": 1.55 * mm});
            skCircle(sketch, "E162", {"center": v(104.5, -296.5) * mm, "radius": 1.55 * mm});
            skCircle(sketch, "E163", {"center": v(-104.5, -296.5) * mm, "radius": 1.55 * mm});
            skLineSegment(sketch, "E164.bottom", {"start": v(15, -167) * mm, "end": v(-15, -167) * mm, "construction": true});
            skLineSegment(sketch, "E164.top", {"start": v(15, -217) * mm, "end": v(-15, -217) * mm, "construction": true});
            skLineSegment(sketch, "E164.left", {"start": v(15, -167) * mm, "end": v(15, -217) * mm, "construction": true});
            skLineSegment(sketch, "E164.right", {"start": v(-15, -167) * mm, "end": v(-15, -217) * mm, "construction": true});
            skLineSegment(sketch, "E165", {"start": v(87.36, -84.5) * mm, "end": v(104.5, -84.5) * mm});
            skLineSegment(sketch, "E166", {"start": v(107.5, -87.5) * mm, "end": v(107.5, -104.65) * mm});
            skPoint(sketch, "E167.visualSharp", {"position": v(107.5, -84.5) * mm});
            skArc(sketch, "E167.filletArc", {"start": v(107.5, -87.5) * mm, "mid": v(106.62, -85.38) * mm, "end": v(104.5, -84.5) * mm});
            skLineSegment(sketch, "E168", {"start": v(87.36, -84.5) * mm, "end": v(13.73, -154.03) * mm});
            skLineSegment(sketch, "E169", {"start": v(107.5, -104.65) * mm, "end": v(38.1, -170.2) * mm});
            skLineSegment(sketch, "E170", {"start": v(87.36, -299.5) * mm, "end": v(104.5, -299.5) * mm});
            skLineSegment(sketch, "E171", {"start": v(107.5, -296.5) * mm, "end": v(107.5, -279.36) * mm});
            skPoint(sketch, "E172.visualSharp", {"position": v(107.5, -299.5) * mm});
            skArc(sketch, "E172.filletArc", {"start": v(104.5, -299.5) * mm, "mid": v(106.62, -298.62) * mm, "end": v(107.5, -296.5) * mm});
            skLineSegment(sketch, "E173", {"start": v(107.5, -279.36) * mm, "end": v(38.1, -213.81) * mm});
            skLineSegment(sketch, "E174", {"start": v(87.36, -299.5) * mm, "end": v(13.73, -229.97) * mm});
            skLineSegment(sketch, "E175", {"start": v(0, -192) * mm, "end": v(0, -167) * mm, "construction": true});
            skLineSegment(sketch, "E176.MirrorCS", {"start": v(-87.36, -84.5) * mm, "end": v(-13.73, -154.03) * mm});
            skLineSegment(sketch, "E177.MirrorCS", {"start": v(-107.5, -104.65) * mm, "end": v(-38.1, -170.2) * mm});
            skLineSegment(sketch, "E178.MirrorCS", {"start": v(-107.5, -279.36) * mm, "end": v(-38.1, -213.81) * mm});
            skLineSegment(sketch, "E179.MirrorCS", {"start": v(-87.36, -299.5) * mm, "end": v(-13.73, -229.97) * mm});
            skLineSegment(sketch, "E180.MirrorCS", {"start": v(-87.36, -299.5) * mm, "end": v(-104.5, -299.5) * mm});
            skArc(sketch, "E181.MirrorCS", {"start": v(-104.5, -299.5) * mm, "mid": v(-106.62, -298.62) * mm, "end": v(-107.5, -296.5) * mm});
            skLineSegment(sketch, "E182.MirrorCS", {"start": v(-107.5, -296.5) * mm, "end": v(-107.5, -279.36) * mm});
            skLineSegment(sketch, "E183.MirrorCS", {"start": v(-87.36, -84.5) * mm, "end": v(-104.5, -84.5) * mm});
            skLineSegment(sketch, "E184.MirrorCS", {"start": v(-107.5, -87.5) * mm, "end": v(-107.5, -104.65) * mm});
            skArc(sketch, "E185.MirrorCS", {"start": v(-107.5, -87.5) * mm, "mid": v(-106.62, -85.38) * mm, "end": v(-104.5, -84.5) * mm});
            skArc(sketch, "E186", {"start": v(-38.1, -213.81) * mm, "mid": v(-28.7, -192) * mm, "end": v(-38.1, -170.2) * mm});
            skArc(sketch, "E187", {"start": v(-13.73, -154.03) * mm, "mid": v(0, -159.5) * mm, "end": v(13.73, -154.03) * mm});
            skArc(sketch, "E188", {"start": v(38.1, -170.2) * mm, "mid": v(28.7, -192) * mm, "end": v(38.1, -213.81) * mm});
            skArc(sketch, "E189", {"start": v(13.73, -229.97) * mm, "mid": v(0, -224.51) * mm, "end": v(-13.73, -229.97) * mm});
            skPoint(sketch, "E190.orphan", {"position": v(-15, -192) * mm});
            skPoint(sketch, "E191.orphan", {"position": v(0, -167) * mm});
            skPoint(sketch, "E192.orphan", {"position": v(15, -192) * mm});
            skPoint(sketch, "E193.orphan", {"position": v(0, -217) * mm});
            skCircle(sketch, "E194", {"center": v(0, -192) * mm, "radius": 2.55 * mm});
            skCircle(sketch, "E195", {"center": v(0, -177) * mm, "radius": 2.55 * mm});
            skCircle(sketch, "E196", {"center": v(0, -207) * mm, "radius": 2.55 * mm});
            skSolve(sketch);
        }
        {
            var Q0;
            Q0 = qSketchRegion(id + "F43", true);
            extrude(context, id + "F44", {"entities" : qUnion([Q0]), "depth" : 3.17 * mm});
        }
        {
            var Q0;
            Q0=makeQuery(id+"F44.opExtrude","CAP_FACE",FACE,{"disambiguationData":[OSD([sQuery(id+"F43.wireOp",EDGE,"E160"),sQuery(id+"F43.wireOp",EDGE,"E161"),sQuery(id+"F43.wireOp",EDGE,"E162"),sQuery(id+"F43.wireOp",EDGE,"E163"),sQuery(id+"F43.wireOp",EDGE,"E165"),sQuery(id+"F43.wireOp",EDGE,"E166"),sQuery(id+"F43.wireOp",EDGE,"E167.filletArc"),sQuery(id+"F43.wireOp",EDGE,"E168"),sQuery(id+"F43.wireOp",EDGE,"E169"),sQuery(id+"F43.wireOp",EDGE,"E170"),sQuery(id+"F43.wireOp",EDGE,"E171"),sQuery(id+"F43.wireOp",EDGE,"E172.filletArc"),sQuery(id+"F43.wireOp",EDGE,"E173"),sQuery(id+"F43.wireOp",EDGE,"E174"),sQuery(id+"F43.wireOp",EDGE,"E176.MirrorCS"),sQuery(id+"F43.wireOp",EDGE,"E177.MirrorCS"),sQuery(id+"F43.wireOp",EDGE,"E178.MirrorCS"),sQuery(id+"F43.wireOp",EDGE,"E179.MirrorCS"),sQuery(id+"F43.wireOp",EDGE,"E180.MirrorCS"),sQuery(id+"F43.wireOp",EDGE,"E181.MirrorCS"),sQuery(id+"F43.wireOp",EDGE,"E182.MirrorCS"),sQuery(id+"F43.wireOp",EDGE,"E183.MirrorCS"),sQuery(id+"F43.wireOp",EDGE,"E184.MirrorCS"),sQuery(id+"F43.wireOp",EDGE,"E185.MirrorCS"),sQuery(id+"F43.wireOp",EDGE,"E186"),sQuery(id+"F43.wireOp",EDGE,"E187"),sQuery(id+"F43.wireOp",EDGE,"E188"),sQuery(id+"F43.wireOp",EDGE,"E189"),sQuery(id+"F43.wireOp",EDGE,"E194"),sQuery(id+"F43.wireOp",EDGE,"E195"),sQuery(id+"F43.wireOp",EDGE,"E196")])],"isStart":true});
            var sketch = newSketch(context, id + "F45", { "sketchPlane" : qUnion([Q0])});
            skLineSegment(sketch, "E197.bottom", {"start": v(2.5, 217.05) * mm, "end": v(-2.5, 217.05) * mm});
            skLineSegment(sketch, "E197.top", {"start": v(2.5, 222.05) * mm, "end": v(-2.5, 222.05) * mm});
            skLineSegment(sketch, "E197.left", {"start": v(2.5, 217.05) * mm, "end": v(2.5, 222.05) * mm});
            skLineSegment(sketch, "E197.right", {"start": v(-2.5, 217.05) * mm, "end": v(-2.5, 222.05) * mm});
            skPoint(sketch, "E197.middle", {"position": v(0, 219.55) * mm});
            skSolve(sketch);
        }
        {
            var Q0;
            Q0 = qSketchRegion(id + "F45", true);
            extrude(context, id + "F46", {"entities" : qUnion([Q0]), "operationType" : NewBodyOperationType.ADD, "depth" : 2 * mm});
        }
        {
            var Q0;
            {var subQ0=makeQuery(id+"F1.opExtrude","CAP_FACE",FACE,{"disambiguationData":[OSD([sQuery(id+"F0.wireOp",EDGE,"E0"),sQuery(id+"F0.wireOp",EDGE,"E1"),sQuery(id+"F0.wireOp",EDGE,"E2"),sQuery(id+"F0.wireOp",EDGE,"E3"),sQuery(id+"F0.wireOp",EDGE,"E4"),sQuery(id+"F0.wireOp",EDGE,"E5"),sQuery(id+"F0.wireOp",EDGE,"E6"),sQuery(id+"F0.wireOp",EDGE,"E7"),sQuery(id+"F0.wireOp",EDGE,"E8"),sQuery(id+"F0.wireOp",EDGE,"E9"),sQuery(id+"F0.wireOp",EDGE,"E10"),sQuery(id+"F0.wireOp",EDGE,"E11.filletArc"),sQuery(id+"F0.wireOp",EDGE,"E12"),sQuery(id+"F0.wireOp",EDGE,"E14.trimOffspring"),sQuery(id+"F0.wireOp",EDGE,"E15.filletArc"),sQuery(id+"F0.wireOp",EDGE,"E16.filletArc")])],"isStart":true});Q0=makeQuery(id+"F17.boolean.opBoolean","MERGE",FACE,{"derivedFrom":[subQ0,makeQuery(id+"F17.opPattern","COPY",FACE,{"derivedFrom":subQ0,"instanceName":"1"})]});}
            var sketch = newSketch(context, id + "F47", { "sketchPlane" : qUnion([Q0])});
            skArc(sketch, "E198", {"start": v(25, 42.5) * mm, "mid": v(30.3, 55.3) * mm, "end": v(17.5, 50) * mm});
            skArc(sketch, "E199", {"start": v(17.5, 50) * mm, "mid": v(4.7, 55.3) * mm, "end": v(10, 42.5) * mm});
            skArc(sketch, "E200", {"start": v(-10, 42.5) * mm, "mid": v(-4.7, 55.3) * mm, "end": v(-17.5, 50) * mm});
            skArc(sketch, "E201", {"start": v(-17.5, 50) * mm, "mid": v(-30.3, 55.3) * mm, "end": v(-25, 42.5) * mm});
            skLineSegment(sketch, "E202.0.8", {"start": v(25, 42.5) * mm, "end": v(25, 50) * mm});
            skLineSegment(sketch, "E202.0.9", {"start": v(25, 50) * mm, "end": v(10, 50) * mm});
            skLineSegment(sketch, "E202.0.14", {"start": v(-10, 42.5) * mm, "end": v(-10, 50) * mm});
            skLineSegment(sketch, "E202.0.15", {"start": v(-10, 50) * mm, "end": v(-25, 50) * mm});
            skLineSegment(sketch, "E202.0.16", {"start": v(-25, 50) * mm, "end": v(-25, 42.5) * mm});
            skLineSegment(sketch, "E203", {"start": v(10, 50) * mm, "end": v(10, 42.5) * mm});
            skSolve(sketch);
        }
        {
            var Q0;
            Q0 = qSketchRegion(id + "F47", true);
            extrude(context, id + "F48", {"entities" : qUnion([Q0]), "operationType" : NewBodyOperationType.ADD, "oppositeDirection" : true, "depth" : .5 * mm, "offsetDistance" : 25 * mm});
        }
    });
